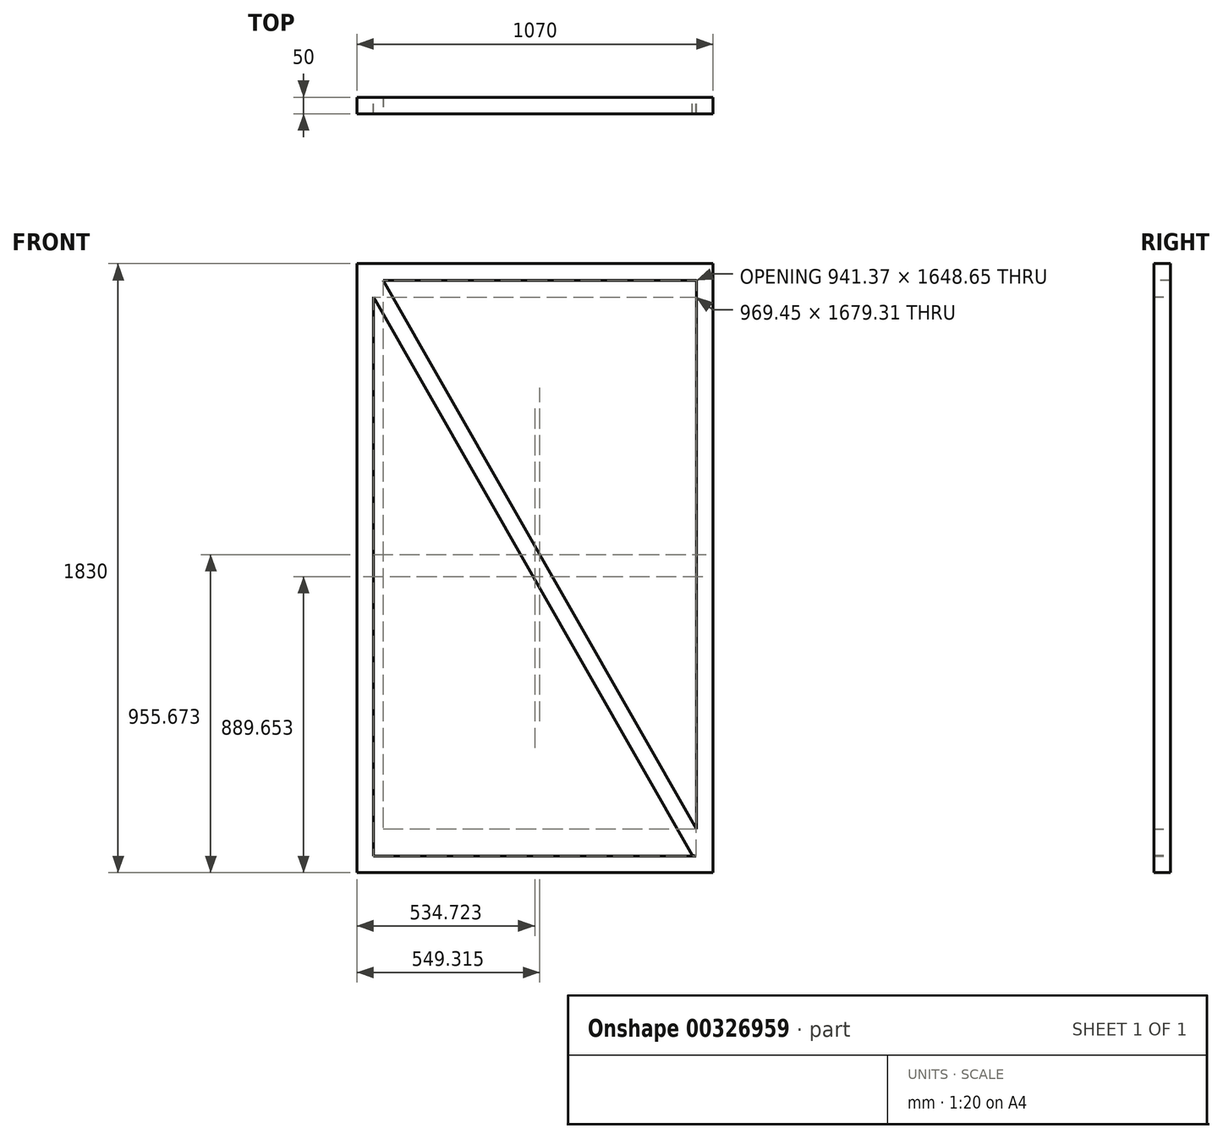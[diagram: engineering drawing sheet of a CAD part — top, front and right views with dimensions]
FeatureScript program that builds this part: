
annotation { "Feature Type Name" : "Feature", "Feature Type Description" : "" }
export const myFeature = defineFeature(function(context is Context, id is Id, definition is map)
    precondition{}
    {
        {
            var Q0;
            Q0=qCreatedBy(makeId("Front.planeOp"),FACE);
            var sketch = newSketch(context, id + "F0", { "sketchPlane" : qUnion([Q0])});
            skLineSegment(sketch, "E0", {"start": v(0, 0) * mm, "end": v(1070, 0) * mm});
            skLineSegment(sketch, "E1", {"start": v(1070, 0) * mm, "end": v(1070, -1830) * mm});
            skLineSegment(sketch, "E2", {"start": v(1070, -1830) * mm, "end": v(0, -1830) * mm});
            skLineSegment(sketch, "E3", {"start": v(0, -1830) * mm, "end": v(0, 0) * mm});
            skLineSegment(sketch, "E4", {"start": v(1070, 0) * mm, "end": v(1020, 0) * mm});
            skLineSegment(sketch, "E5", {"start": v(1020, 0) * mm, "end": v(1020, -50) * mm});
            skLineSegment(sketch, "E6", {"start": v(1020, -50) * mm, "end": v(50, -50) * mm});
            skLineSegment(sketch, "E7", {"start": v(50, -50) * mm, "end": v(50, -1780) * mm});
            skLineSegment(sketch, "E8", {"start": v(50, -1780) * mm, "end": v(1020, -1780) * mm});
            skLineSegment(sketch, "E9", {"start": v(1020, -1780) * mm, "end": v(1020, -50) * mm});
            skSolve(sketch);
        }
        {
            var Q0;
            Q0 = qSketchRegion(id + "F0", true);
            extrude(context, id + "F1", {"entities" : qUnion([Q0]), "depth" : 50 * mm});
        }
        {
            var Q0;
            Q0=qCreatedBy(makeId("Front.planeOp"),FACE);
            var sketch = newSketch(context, id + "F2", { "sketchPlane" : qUnion([Q0])});
            skLineSegment(sketch, "E10", {"start": v(842.64, -1388.04) * mm, "end": v(1041.9, -1737) * mm});
            skLineSegment(sketch, "E11", {"start": v(1041.9, -1737) * mm, "end": v(1039.5, -1783.23) * mm});
            skLineSegment(sketch, "E12", {"start": v(842.64, -1388.04) * mm, "end": v(78.3, -49.42) * mm});
            skLineSegment(sketch, "E13", {"start": v(78.3, -49.42) * mm, "end": v(49.82, -49.97) * mm});
            skLineSegment(sketch, "E14", {"start": v(861.88, -1522.57) * mm, "end": v(1007.8, -1778.12) * mm});
            skLineSegment(sketch, "E15", {"start": v(1007.8, -1778.12) * mm, "end": v(1039.5, -1783.23) * mm});
            skLineSegment(sketch, "E16", {"start": v(861.88, -1522.57) * mm, "end": v(155.7, -285.83) * mm});
            skLineSegment(sketch, "E17", {"start": v(155.7, -285.83) * mm, "end": v(47.82, -96.87) * mm});
            skLineSegment(sketch, "E18", {"start": v(47.82, -96.87) * mm, "end": v(49.82, -49.97) * mm});
            skSolve(sketch);
        }
        {
            var Q0;
            Q0 = qSketchRegion(id + "F2", true);
            extrude(context, id + "F3", {"entities" : qUnion([Q0]), "operationType" : NewBodyOperationType.ADD, "depth" : 50 * mm});
        }
    });
